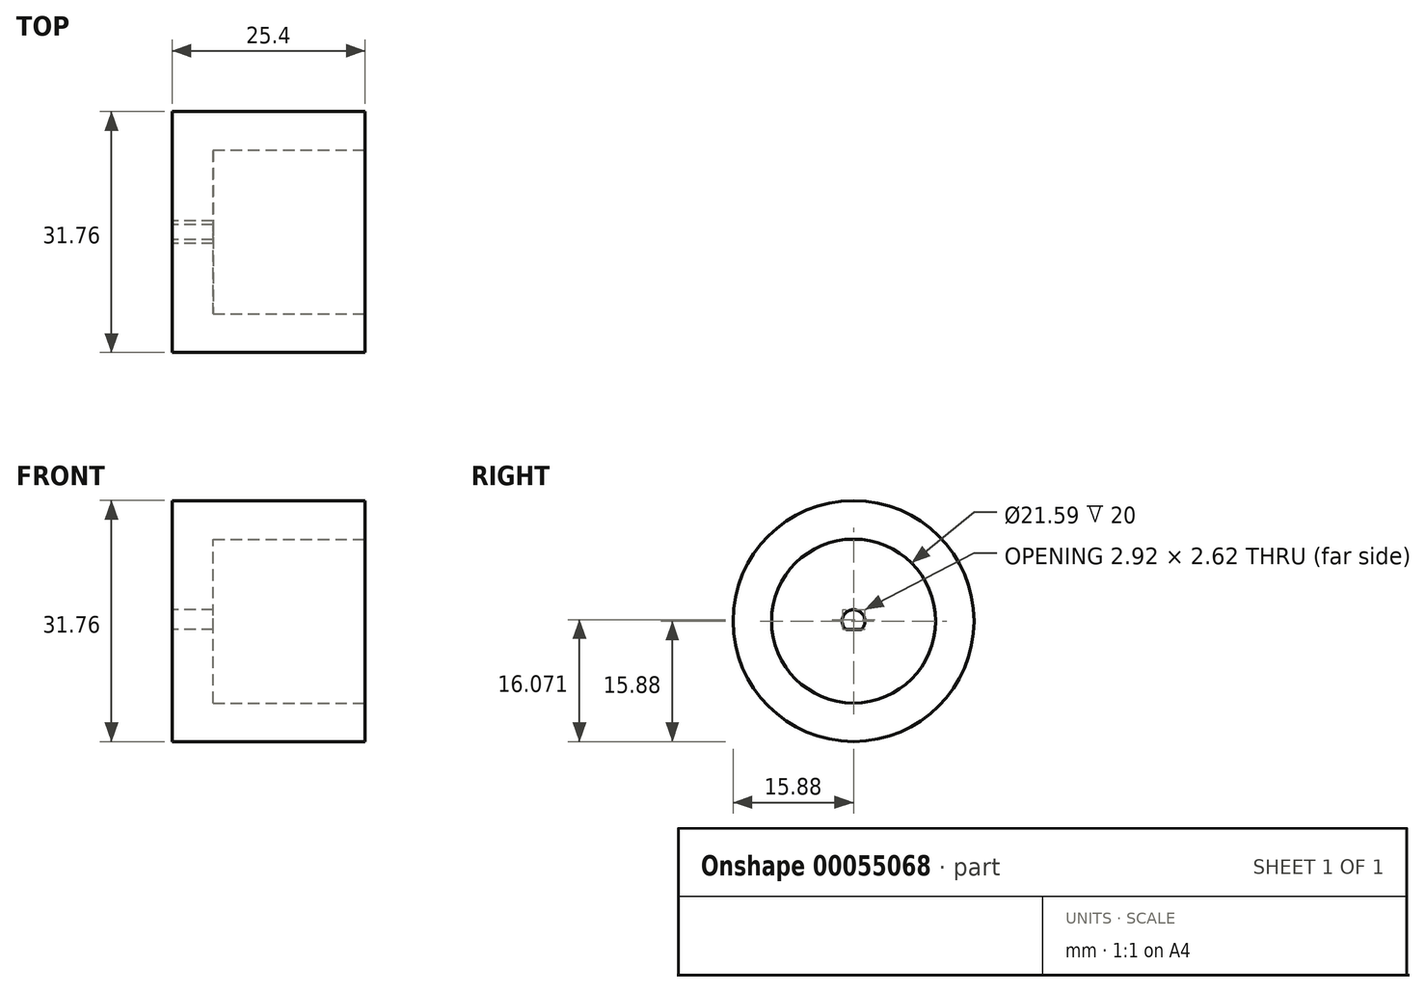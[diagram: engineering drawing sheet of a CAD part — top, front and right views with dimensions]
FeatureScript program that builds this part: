
annotation { "Feature Type Name" : "Feature", "Feature Type Description" : "" }
export const myFeature = defineFeature(function(context is Context, id is Id, definition is map)
    precondition{}
    {
        {
            var Q0;
            Q0=qCreatedBy(makeId("Right.planeOp"),FACE);
            var sketch = newSketch(context, id + "F0", { "sketchPlane" : qUnion([Q0])});
            skCircle(sketch, "E0", {"center": v(0, 0) * mm, "radius": 15.88 * mm});
            skArc(sketch, "E1", {"start": v(-1, -1.12) * mm, "mid": v(0, 1.5) * mm, "end": v(1, -1.12) * mm});
            skLineSegment(sketch, "E2", {"start": v(1, -1.12) * mm, "end": v(-1, -1.12) * mm});
            skSolve(sketch);
        }
        {
            var Q0;
            Q0=makeQuery(id+"F0.imprint","IMPRINT",FACE,{"disambiguationData":[TD([[makeQuery(id+"F0.imprint","IMPRINT",EDGE,{"derivedFrom":sQuery(id+"F0.wireOp",EDGE,"E0")}),1.0]])]});
            extrude(context, id + "F1", {"entities" : qUnion([Q0]), "depth" : 25.4 * mm});
        }
        {
            var Q0;
            Q0=makeQuery(id+"F1.opExtrude","CAP_FACE",FACE,{"disambiguationData":[OSD([sQuery(id+"F0.wireOp",EDGE,"E0"),sQuery(id+"F0.wireOp",EDGE,"E1"),sQuery(id+"F0.wireOp",EDGE,"E2")])],"isStart":false});
            var sketch = newSketch(context, id + "F2", { "sketchPlane" : qUnion([Q0])});
            skCircle(sketch, "E3", {"center": v(0, 0) * mm, "radius": 10.8 * mm});
            skLineSegment(sketch, "E4", {"start": v(0, -15.88) * mm, "end": v(0, -10.8) * mm, "construction": true});
            skSolve(sketch);
        }
        {
            var Q0;
            Q0=qSketchRegion(id+"F2",true);
            extrude(context, id + "F3", {"entities" : qUnion([Q0]), "operationType" : NewBodyOperationType.REMOVE, "oppositeDirection" : true, "depth" : 20 * mm});
        }
    });
